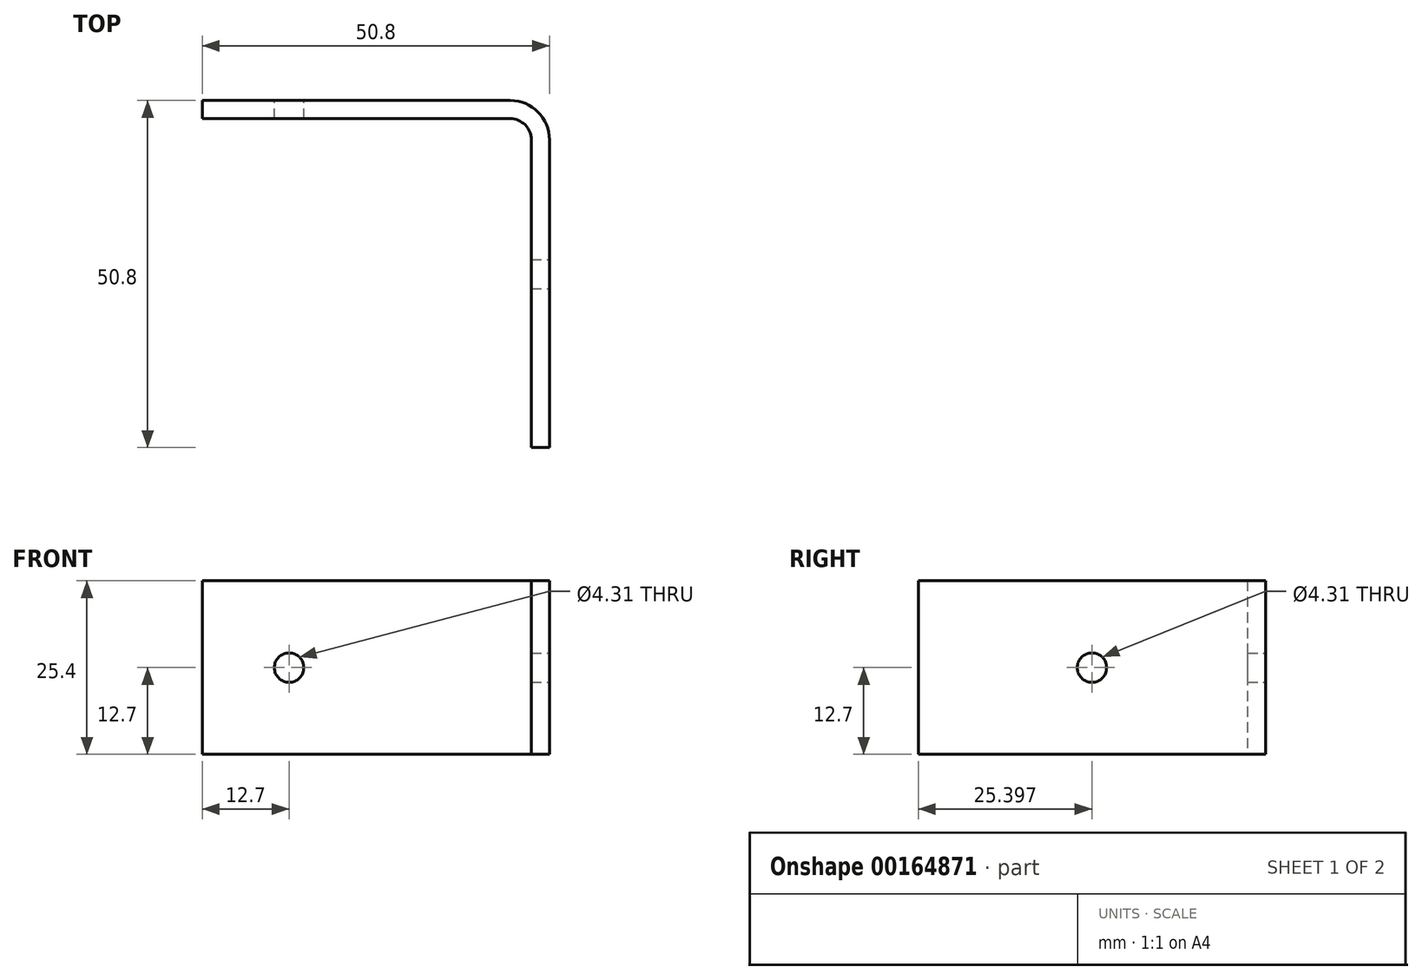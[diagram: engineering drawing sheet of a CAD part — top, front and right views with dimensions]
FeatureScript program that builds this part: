
annotation { "Feature Type Name" : "Feature", "Feature Type Description" : "" }
export const myFeature = defineFeature(function(context is Context, id is Id, definition is map)
    precondition{}
    {
        {
            var Q0;
            Q0=qCreatedBy(makeId("Top.planeOp"),FACE);
            var sketch = newSketch(context, id + "F0", { "sketchPlane" : qUnion([Q0])});
            skLineSegment(sketch, "E0.bottom", {"start": v(0, 0) * mm, "end": v(48.14, 0) * mm});
            skLineSegment(sketch, "E0.top", {"start": v(0, 2.66) * mm, "end": v(50.8, 2.66) * mm});
            skLineSegment(sketch, "E0.left", {"start": v(0, 0) * mm, "end": v(0, 2.66) * mm});
            skLineSegment(sketch, "E1.top", {"start": v(48.14, -48.14) * mm, "end": v(50.8, -48.14) * mm});
            skLineSegment(sketch, "E1.left", {"start": v(48.14, 0) * mm, "end": v(48.14, -48.14) * mm});
            skLineSegment(sketch, "E1.right", {"start": v(50.8, 2.66) * mm, "end": v(50.8, -48.14) * mm});
            skSolve(sketch);
        }
        {
            var Q0;
            Q0=qSketchRegion(id+"F0",true);
            extrude(context, id + "F1", {"entities" : qUnion([Q0]), "depth" : 25.4 * mm});
        }
        {
            var Q0;
            Q0=makeQuery(id+"F1.opExtrude","SWEPT_FACE",FACE,{"disambiguationData":[OSD([sQuery(id+"F0.wireOp",EDGE,"E0.top")])]});
            var sketch = newSketch(context, id + "F2", { "sketchPlane" : qUnion([Q0])});
            skLineSegment(sketch, "E2.bottom", {"start": v(0, 12.7) * mm, "end": v(-12.7, 12.7) * mm, "construction": true});
            skLineSegment(sketch, "E2.top", {"start": v(0, 25.4) * mm, "end": v(-12.7, 25.4) * mm, "construction": true});
            skLineSegment(sketch, "E2.left", {"start": v(0, 12.7) * mm, "end": v(0, 25.4) * mm, "construction": true});
            skLineSegment(sketch, "E2.right", {"start": v(-12.7, 12.7) * mm, "end": v(-12.7, 25.4) * mm, "construction": true});
            skCircle(sketch, "E3", {"center": v(-12.7, 12.7) * mm, "radius": 2.15 * mm});
            skSolve(sketch);
        }
        {
            var Q0;
            Q0=qSketchRegion(id+"F2",true);
            var Q1;
            Q1=makeQuery(id+"F1.opExtrude","SWEPT_FACE",FACE,{"disambiguationData":[OSD([sQuery(id+"F0.wireOp",EDGE,"E0.bottom")])]});
            extrude(context, id + "F3", {"entities" : qUnion([Q0]), "operationType" : NewBodyOperationType.REMOVE, "endBound" : BoundingType.UP_TO_SURFACE, "oppositeDirection" : true, "endBoundEntityFace" : qUnion([Q1]), "depth" : 25.4 * mm});
        }
        {
            var Q0;
            Q0=makeQuery(id+"F1.opExtrude","SWEPT_FACE",FACE,{"disambiguationData":[OSD([sQuery(id+"F0.wireOp",EDGE,"E1.right")])]});
            var sketch = newSketch(context, id + "F4", { "sketchPlane" : qUnion([Q0])});
            skLineSegment(sketch, "E4.bottom", {"start": v(-48.14, 12.7) * mm, "end": v(-22.74, 12.7) * mm, "construction": true});
            skLineSegment(sketch, "E4.top", {"start": v(-48.14, 25.4) * mm, "end": v(-22.74, 25.4) * mm, "construction": true});
            skLineSegment(sketch, "E4.left", {"start": v(-48.14, 12.7) * mm, "end": v(-48.14, 25.4) * mm, "construction": true});
            skLineSegment(sketch, "E4.right", {"start": v(-22.74, 12.7) * mm, "end": v(-22.74, 25.4) * mm, "construction": true});
            skCircle(sketch, "E5", {"center": v(-22.74, 12.7) * mm, "radius": 2.15 * mm});
            skSolve(sketch);
        }
        {
            var Q0;
            Q0=qSketchRegion(id+"F4",true);
            var Q1;
            Q1=makeQuery(id+"F1.opExtrude","SWEPT_FACE",FACE,{"disambiguationData":[OSD([sQuery(id+"F0.wireOp",EDGE,"E1.left")])]});
            extrude(context, id + "F5", {"entities" : qUnion([Q0]), "operationType" : NewBodyOperationType.REMOVE, "endBound" : BoundingType.UP_TO_SURFACE, "oppositeDirection" : true, "endBoundEntityFace" : qUnion([Q1]), "depth" : 25.4 * mm});
        }
        {
            var Q0;
            Q0=makeQuery(id+"F1.opExtrude","SWEPT_EDGE",EDGE,{"disambiguationData":[OSD([sQuery(id+"F0.wireOp",EDGE,"E0.bottom"),sQuery(id+"F0.wireOp",EDGE,"E1.left")])]});
            fillet(context, id + "F6", {"entities" : qUnion([Q0]), "radius" : 3.08 * mm, "tangentPropagation" : true, "allowEdgeOverflow" : false});
        }
        {
            var Q0;
            Q0=makeQuery(id+"F1.opExtrude","SWEPT_EDGE",EDGE,{"disambiguationData":[OSD([sQuery(id+"F0.wireOp",EDGE,"E0.top"),sQuery(id+"F0.wireOp",EDGE,"E1.right")])]});
            fillet(context, id + "F7", {"entities" : qUnion([Q0]), "radius" : 5.74 * mm, "tangentPropagation" : true, "allowEdgeOverflow" : false});
        }
    });
